# Revit family: 873-00-001-DN350-400
name_source: partatom
category: Generic Models
units: mm (PartAtom-declared; Revit-internal decimal feet)

## family parameters
Always vertical = Yes
Can host rebar = No
Cut with Voids When Loaded = No
Part Type = Normal
Room Calculation Point = No
Round Connector Dimension = Use Diameter
Shared = No
Work Plane-Based = No

## types (4) — shared parameters
873-0350-00-041000 = DN350_PN10
873-0350-00-141000 = DN350_PN16
873-0400-00-041000 = DN400_PN10
873-0400-00-141000 = DN400_PN16
Angle = 22.50°
Body_Wallthicknss = 10 mm  [stored 0.0328084 ft]
Description_ = AVK DISMANTLING JOINT
Flange_thickness = 20 mm  [stored 0.0656168 ft]
Search_table = 873-00-001-DN350-400
URL product pages = https://www.avkvalves.com

## per-type parameters (varying)
| type | A | DN | Id(Radius) | L | T | d1 | d2 |
| DN350_PN10 | 240 mm  [stored 0.787402 ft] | 350 mm  [stored 1.14829 ft] | 175 mm  [stored 0.574147 ft] | 400 mm  [stored 1.31234 ft] | 20 mm  [stored 0.0656168 ft] | 460 mm  [stored 1.50919 ft] | 253 mm |
| DN350_PN16 | 240 mm  [stored 0.787402 ft] | 350 mm  [stored 1.14829 ft] | 175 mm  [stored 0.574147 ft] | 410 mm  [stored 1.34514 ft] | 24 mm  [stored 0.0787402 ft] | 470 mm  [stored 1.54199 ft] | 260 mm  [stored 0.853018 ft] |
| DN400_PN10 | 250 mm  [stored 0.82021 ft] | 400 mm  [stored 1.31234 ft] | 200 mm  [stored 0.656168 ft] | 420 mm  [stored 1.37795 ft] | 24 mm  [stored 0.0787402 ft] | 515 mm  [stored 1.68963 ft] | 283 mm |
| DN400_PN16 | 250 mm  [stored 0.82021 ft] | 400 mm  [stored 1.31234 ft] | 200 mm  [stored 0.656168 ft] | 430 mm | 27 mm  [stored 0.0885827 ft] | 525 mm  [stored 1.72244 ft] | 290 mm  [stored 0.951444 ft] |

note: [stored X ft] marks values corroborated as IEEE doubles in the binary element streams (Revit-internal decimal feet)

## geometry (parser evidence)
native form markers: Sweep x4
no freeform markers — native parametric forms only
